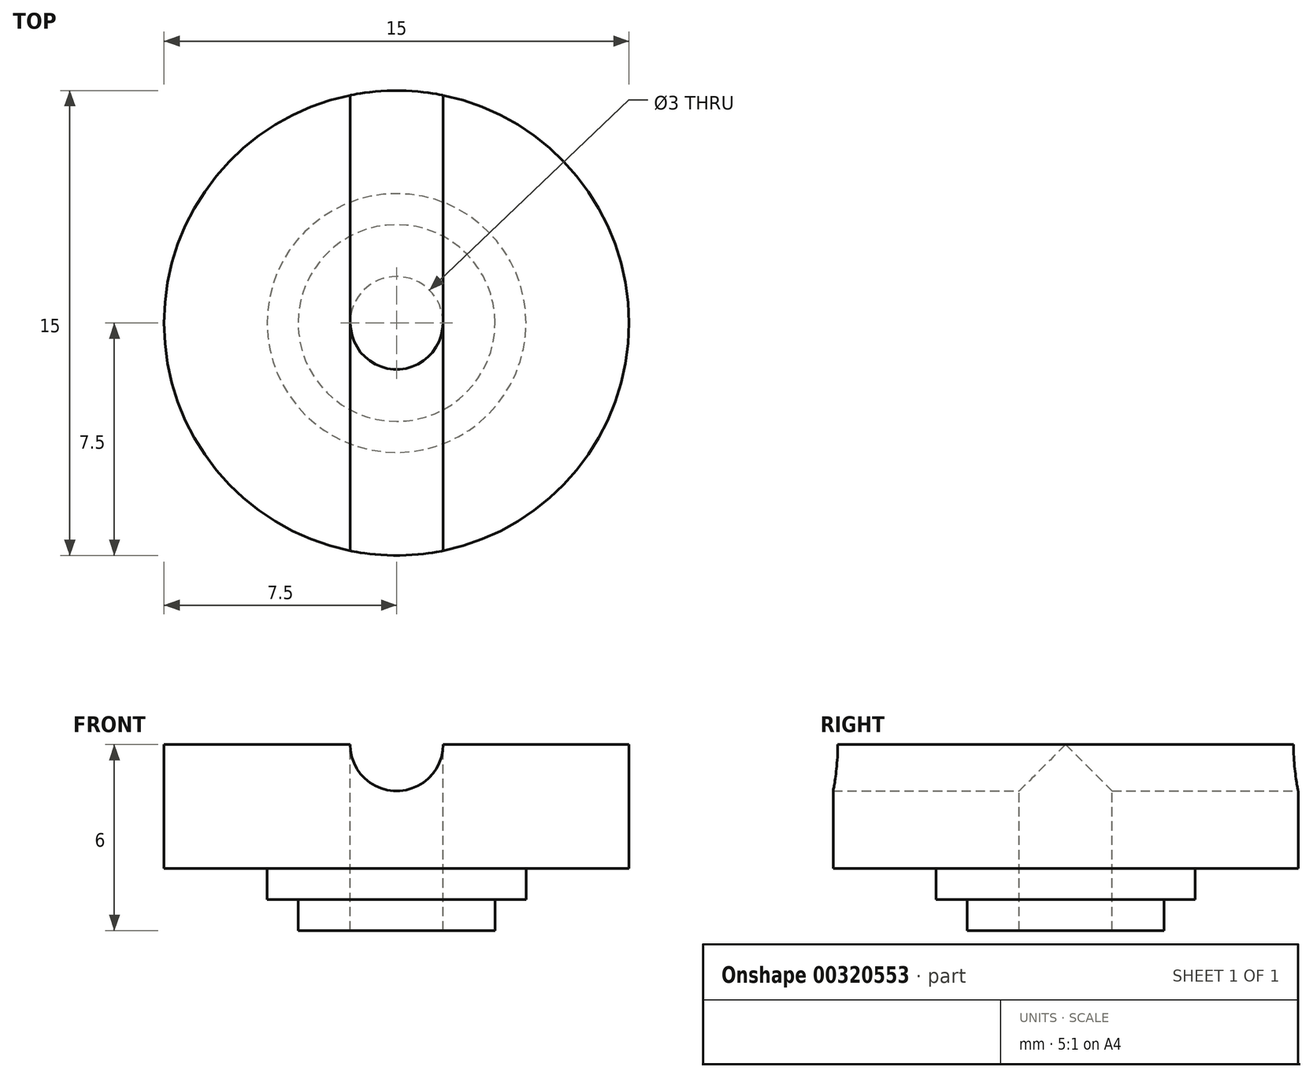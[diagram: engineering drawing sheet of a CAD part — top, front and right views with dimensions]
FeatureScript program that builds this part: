
annotation { "Feature Type Name" : "Feature", "Feature Type Description" : "" }
export const myFeature = defineFeature(function(context is Context, id is Id, definition is map)
    precondition{}
    {
        {
            var Q0;
            Q0=qCreatedBy(makeId("Front.planeOp"),FACE);
            var sketch = newSketch(context, id + "F0", { "sketchPlane" : qUnion([Q0])});
            skLineSegment(sketch, "E0", {"start": v(1.5, 0) * mm, "end": v(1.5, -6) * mm});
            skLineSegment(sketch, "E1", {"start": v(1.5, -6) * mm, "end": v(3.17, -6) * mm});
            skLineSegment(sketch, "E2", {"start": v(3.17, -6) * mm, "end": v(3.17, -5) * mm});
            skLineSegment(sketch, "E3", {"start": v(3.17, -5) * mm, "end": v(4.17, -5) * mm});
            skLineSegment(sketch, "E4", {"start": v(4.17, -5) * mm, "end": v(4.17, -4) * mm});
            skLineSegment(sketch, "E5", {"start": v(4.17, -4) * mm, "end": v(7.5, -4) * mm});
            skLineSegment(sketch, "E6", {"start": v(7.5, -4) * mm, "end": v(7.5, 0) * mm});
            skLineSegment(sketch, "E7", {"start": v(7.5, 0) * mm, "end": v(1.5, 0) * mm});
            skLineSegment(sketch, "E8", {"start": v(0, 0) * mm, "end": v(0, -7.48) * mm, "construction": true});
            skSolve(sketch);
        }
        {
            var Q0;
            Q0=qCreatedBy(makeId("Front.planeOp"),FACE);
            var sketch = newSketch(context, id + "F1", { "sketchPlane" : qUnion([Q0])});
            skLineSegment(sketch, "E9", {"start": v(0, 0) * mm, "end": v(0, -10.3) * mm, "construction": true});
            skSolve(sketch);
        }
        {
            var Q0;
            Q0=makeQuery(id+"F0.imprint","IMPRINT",FACE,{"disambiguationData":[TD([[makeQuery(id+"F0.imprint","IMPRINT",EDGE,{"derivedFrom":sQuery(id+"F0.wireOp",EDGE,"E0")}),1.0]])]});
            var Q1;
            Q1=sQuery(id+"F1.wireOp",EDGE,"E9");
            revolve(context, id + "F2", {"entities" : qUnion([Q0]), "axis" : qUnion([Q1]), "revolveType" : RevolveType.FULL});
        }
        {
            var Q0;
            Q0=qCreatedBy(makeId("Front.planeOp"),FACE);
            var sketch = newSketch(context, id + "F3", { "sketchPlane" : qUnion([Q0])});
            skCircle(sketch, "E10", {"center": v(0, 0) * mm, "radius": 1.5 * mm});
            skSolve(sketch);
        }
        {
            var Q0;
            Q0 = qSketchRegion(id + "F3", true);
            extrude(context, id + "F4", {"entities" : qUnion([Q0]), "operationType" : NewBodyOperationType.REMOVE, "endBound" : BoundingType.SYMMETRIC, "depth" : 25 * mm});
        }
    });
